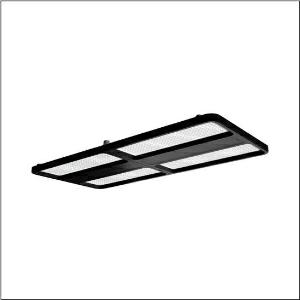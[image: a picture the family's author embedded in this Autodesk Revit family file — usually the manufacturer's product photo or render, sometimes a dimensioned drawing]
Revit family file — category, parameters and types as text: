
# Revit family: highbay_21_maxi_52hn32db4tda
name_source: partatom
category: Lighting Fixtures
units: mm (PartAtom-declared; Revit-internal decimal feet)

## family parameters
Cut with Voids When Loaded = No
Host = Face
Light Source = No
Part Type = Normal
Room Calculation Point = No
Round Connector Dimension = Use Diameter
Shared = No

## types (1)
- --- (1 x LED, 8350 lm, 44.8 W, 4000K)
    Apparent Load = 45 VA
    CIE Flux Codes = 90 98 100 100 100
    Color Rendering = 80
    Color Temperature = 4000K
    Default Elevation = 1800 mm
    Description = high bay luminaire Highbay 21 maxi; direct symmetric wide distribution, light control with lens of PMMA; UGR ≤ 22 (X = 4H | Y = 8H | S = 0.25H | reflection values 70/50/20); luminous flux: 53.000lm; light colour: 840, colour temperature: 4000K, MacAdam ≤ 3 SDCM (initial), colour rendering: CRI > 80; luminous efficacy: 184,9lm/W; rated service life: 75.000h (L80) at AT= ta max; control: DALI 2; luminaire connection: terminal, 5-pole, max. 2.5mm² (cable entry for one cable, Ø 8.5..16mm); mains connection: 230..240V, AC/DC 0/50..60Hz; connected load: 286,6W; protection rating (complete): IP66; insulation class (complete): insulation class I (protective earthing); protection symbol: D; impact resistance: IK08; certification: CE, ENEC, VDE, UKCA; luminaire for central battery installations according to EN 60598-2-22, internal wiring halogen-free; luminaire LABS conformity tested according to VDMA 24364:2018-05; Suitable for use in the food industry according to the specifications of IFS-Food, HACCP and/or BRC; housing frame of high-performance plastic PA6, matt jet black (RAL 9005); cover of PMMA; dimension (LxWxH): 946 x 442 x 72mm; permissible operating ambient temperature: -40..+55°C (reducing of maximum allowable ambient temperature of 5°C with ceiling mounting); packaging unit: 1 piece; (delivery without accessories; please order mounting accessories separately)
    Height = 72 mm  [stored 0.23622 ft]
    Lamp = 1 x LED
    Lamp Light Flux = 8350 lm
    Lamp Power = 44.8 W
    Lamp count = 1
    Length = 946 mm
    Luminous efficacy = 186 lm/W
    Manufacturer = Siteco
    ModVariant = No
    Model = 52HN32DB4TDA
    Mounting Place = Ceiling
    Mounting Type = Pendant
    Number of Poles = 1
    OnlyDefault = Yes
    Power Factor = 1
    Product Name = Highbay 21 maxi
    Product group = high bay luminaire
    ProductGroupID = 902
    Protection Class = Protection class I
    Protection Degree = IP 66
    RLX_Detail_Level = 1
    RLX_Emergency_Light_Flux = 0 lm
    RLX_Emergency_Type = 0
    RLX_Emergency_Type_DB = No
    RlxData = <blob elided: 133553 chars, md5=b120a13c>
    Socket = socket
    Standby Power = 0 W
    System Light Flux = 8350 lm
    System Power = 45 W
    Type Comments = : DC mode (central or group accumulator) initial emergency light level
    Type Image = l_1378821.jpg
    URL = http://relux.com
    VarID = @adj_019267
    Voltage = 0 V
    Weight = 0.00 kg
    Width = 442 mm

note: [stored X ft] marks values corroborated as IEEE doubles in the binary element streams (Revit-internal decimal feet)

## geometry (parser evidence)
native form markers: Blend x4, Sweep x9
no freeform markers — native parametric forms only
